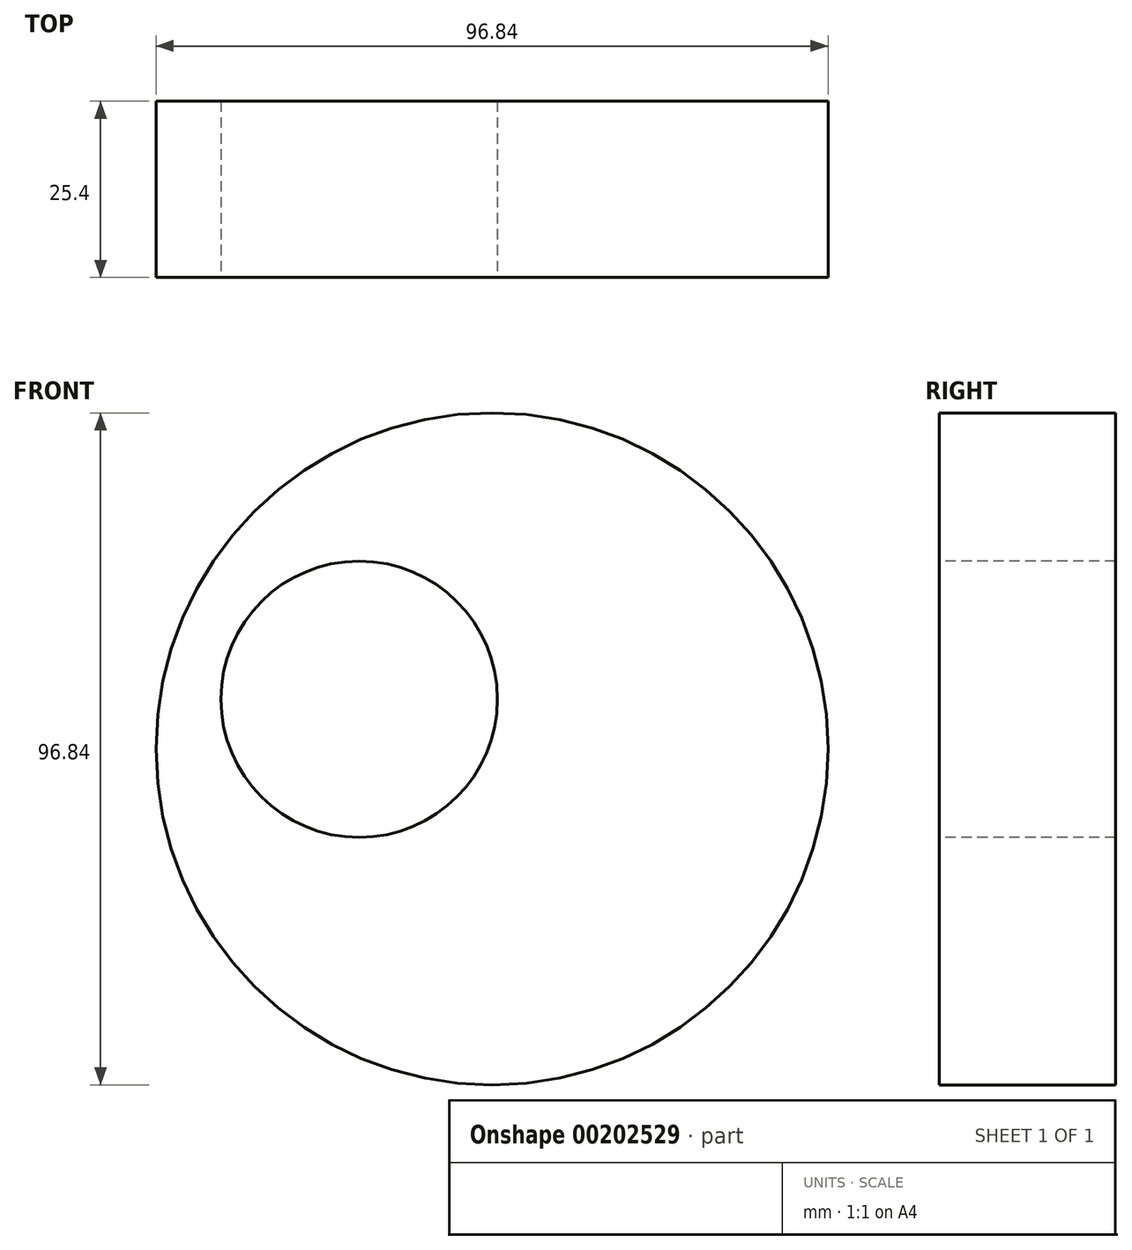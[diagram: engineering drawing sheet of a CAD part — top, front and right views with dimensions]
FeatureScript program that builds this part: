
annotation { "Feature Type Name" : "Feature", "Feature Type Description" : "" }
export const myFeature = defineFeature(function(context is Context, id is Id, definition is map)
    precondition{}
    {
        {
            var Q0;
            Q0=qCreatedBy(makeId("Front.planeOp"),FACE);
            var sketch = newSketch(context, id + "F0", { "sketchPlane" : qUnion([Q0])});
            skCircle(sketch, "E0", {"center": v(0, 0) * mm, "radius": 48.42 * mm});
            skCircle(sketch, "E1", {"center": v(-19.15, 7.15) * mm, "radius": 19.91 * mm});
            skSolve(sketch);
        }
        {
            var Q0;
            Q0=makeQuery(id+"F0.imprint","IMPRINT",FACE,{"disambiguationData":[TD([[makeQuery(id+"F0.imprint","IMPRINT",EDGE,{"derivedFrom":sQuery(id+"F0.wireOp",EDGE,"E0")}),1.0]])]});
            var Q1;
            Q1=sQuery(id+"F0.wireOp",EDGE,"E0");
            var Q2;
            Q2=sQuery(id+"F0.wireOp",EDGE,"E1");
            extrude(context, id + "F1", {"entities" : qUnion([Q0]), "bodyType" : ToolBodyType.SURFACE, "surfaceEntities" : qUnion([Q1, Q2]), "endBound" : BoundingType.SYMMETRIC, "depth" : 25.4 * mm});
        }
    });
